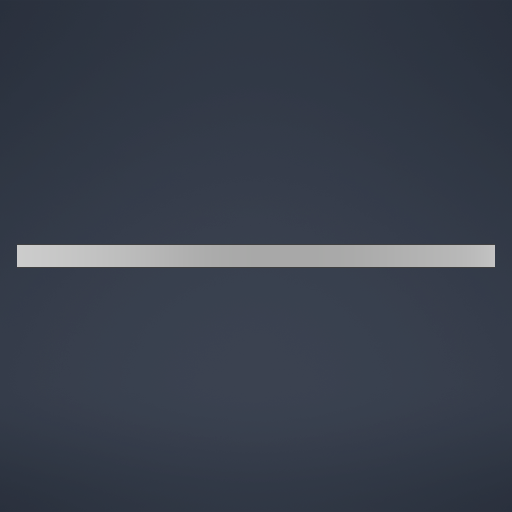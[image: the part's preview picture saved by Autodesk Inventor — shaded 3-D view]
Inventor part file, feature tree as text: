
AUTODESK INVENTOR PART (.ipt)
format: ipt  version: 2025 (Build 290162000, 162)  size: 472,064 bytes
history: native  units: in
note: dims shown in document units (in); Inventor stores cm internally (conversion verified against a paired STEP export)
features: sketch x7, extrude x5, hole x1, revolve x1
ambient origin geometry x8: Origin, YZ Plane, XZ Plane, XY Plane, X Axis, Y Axis, Z Axis, Center Point
bodies: Solid1 (feature_tree)
feature tree (14):
  sketch  "Sketch1"  dims[d0=11.811in d1=7.874in]
  extrude  "Extrusion1"  Depth=7.874in
  extrude  "Extrusion3"  Depth=0.0787in
  extrude  "Extrusion4"  Depth=3.937in TaperAngle=360.0deg
  sketch  "Sketch3"  dims[d14=0.2165in d15=3.937in d17=360.0deg]
  extrude  "Extrusion5"  Depth=11.0236in
  hole  "Hole1"  [1 undecoded]
  revolve  "Revolution1"  [1 undecoded]
  extrude  "Extrusion6"  Depth=0.0837in TaperAngle=0.0deg
  sketch  "Sketch Circular Pattern2"  dims[d8=0.0787in d9=0.0in d13=9.8425in]
  sketch  "Sketch Circular Pattern3"  dims[d19=9.498in d20=11.0236in]
  sketch  "Sketch4"  dims[d21=0.2165in d23=3.937in d25=360.0deg]
  sketch  "Sketch5"  dims[d27=0.1673in d28=0.0in d33=0.4232in d34=0.0in]
  sketch  "Sketch Circular Pattern5"  dims[d35=9.498in d36=0.0837in d37=0.0in d38=0.2165in d39=0.2362in d40=0.4124in d41=0.2904in d42=90.0deg d43=0.315in d44=0.8108in d45=0.1575in d46=0.1575in d48=0.5709in d49=0.1575in d50=0.1575in d51=360.0deg d52=0.3445in d53=0.2224in d54=0.0in d55=7.874in d56=3.937in d58=360.0deg]
note: 2 required parameter values undecoded (feature->parameter linkage not recoverable at this tier; creation-order binding heuristic only, values carry confidence <= 0.55)